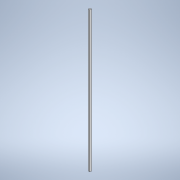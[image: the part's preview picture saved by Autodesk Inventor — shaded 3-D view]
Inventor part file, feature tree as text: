
AUTODESK INVENTOR PART (.ipt)
format: ipt  version: 2022 (Build 260153000, 153)  size: 149,504 bytes
history: native  units: mm
features: extrude x1, sketch x1
ambient origin geometry x8: Origin, YZ Plane, XZ Plane, XY Plane, X Axis, Y Axis, Z Axis, Center Point
bodies: Body1 (feature_tree)
feature tree (2):
  extrude  "Extrusion7"  Depth=5.0mm
  sketch  "Sketch4"  dims[d31=34.456mm d103=5.0mm d104=5.0mm d105=488.0mm d106=0.0mm]
